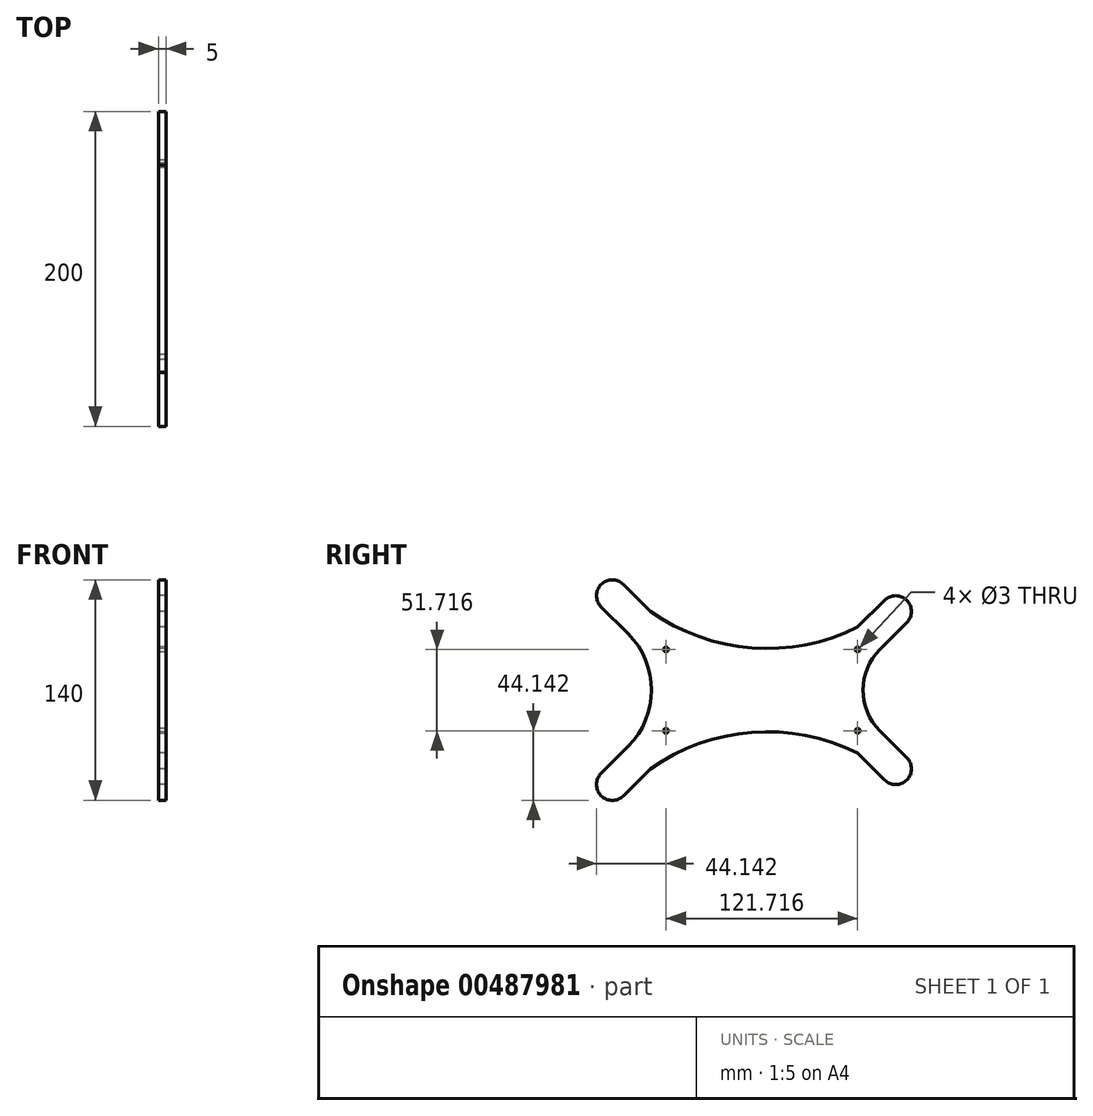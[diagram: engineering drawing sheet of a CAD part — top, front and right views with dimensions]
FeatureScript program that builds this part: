
annotation { "Feature Type Name" : "Feature", "Feature Type Description" : "" }
export const myFeature = defineFeature(function(context is Context, id is Id, definition is map)
    precondition{}
    {
        {
            var Q0;
            Q0=qCreatedBy(makeId("Right.planeOp"),FACE);
            var sketch = newSketch(context, id + "F0", { "sketchPlane" : qUnion([Q0])});
            skLineSegment(sketch, "E0", {"start": v(97.07, 42.93) * mm, "end": v(80, 25.86) * mm});
            skLineSegment(sketch, "E1", {"start": v(82.93, 57.07) * mm, "end": v(65.86, 40) * mm});
            skLineSegment(sketch, "E2.MirrorCS", {"start": v(97.07, -42.93) * mm, "end": v(80, -25.86) * mm});
            skLineSegment(sketch, "E3.MirrorCS", {"start": v(82.93, -57.07) * mm, "end": v(65.86, -40) * mm});
            skLineSegment(sketch, "E4", {"start": v(-82.93, 67.07) * mm, "end": v(-65.86, 50) * mm});
            skLineSegment(sketch, "E5", {"start": v(-97.07, 52.93) * mm, "end": v(-80, 35.86) * mm});
            skLineSegment(sketch, "E6.MirrorCS", {"start": v(-97.07, -52.93) * mm, "end": v(-80, -35.86) * mm});
            skLineSegment(sketch, "E7.MirrorCS", {"start": v(-82.93, -67.07) * mm, "end": v(-65.86, -50) * mm});
            skArc(sketch, "E8", {"start": v(65.86, -40) * mm, "mid": v(-1.38, -26.83) * mm, "end": v(-65.86, -50) * mm});
            skArc(sketch, "E9.MirrorCS", {"start": v(65.86, 40) * mm, "mid": v(-1.38, 26.83) * mm, "end": v(-65.86, 50) * mm});
            skArc(sketch, "E10", {"start": v(80, 25.86) * mm, "mid": v(69.29, 0) * mm, "end": v(80, -25.86) * mm});
            skArc(sketch, "E11", {"start": v(-80, -35.86) * mm, "mid": v(-65.15, 0) * mm, "end": v(-80, 35.86) * mm});
            skArc(sketch, "E12", {"start": v(82.93, -57.07) * mm, "mid": v(97.07, -57.07) * mm, "end": v(97.07, -42.93) * mm});
            skArc(sketch, "E13.MirrorCS", {"start": v(82.93, 57.07) * mm, "mid": v(97.07, 57.07) * mm, "end": v(97.07, 42.93) * mm});
            skArc(sketch, "E14", {"start": v(-97.07, -52.93) * mm, "mid": v(-97.07, -67.07) * mm, "end": v(-82.93, -67.07) * mm});
            skArc(sketch, "E15.MirrorCS", {"start": v(-97.07, 52.93) * mm, "mid": v(-97.07, 67.07) * mm, "end": v(-82.93, 67.07) * mm});
            skCircle(sketch, "E16", {"center": v(65.86, -25.86) * mm, "radius": 1.5 * mm});
            skCircle(sketch, "E17.MirrorC", {"center": v(65.86, 25.86) * mm, "radius": 1.5 * mm});
            skCircle(sketch, "E18", {"center": v(-55.86, -25.86) * mm, "radius": 1.5 * mm});
            skCircle(sketch, "E19.MirrorC", {"center": v(-55.86, 25.86) * mm, "radius": 1.5 * mm});
            skLineSegment(sketch, "E20", {"start": v(-54.36, -25.86) * mm, "end": v(64.36, -25.86) * mm});
            skSolve(sketch);
        }
        {
            var Q0;
            Q0=makeQuery(id+"F0.imprint","IMPRINT",FACE,{"disambiguationData":[TD([[makeQuery(id+"F0.imprint","IMPRINT",EDGE,{"derivedFrom":sQuery(id+"F0.wireOp",EDGE,"E0")}),-1.0]])]});
            extrude(context, id + "F1", {"entities" : qUnion([Q0]), "offsetDistance" : 25 * mm, "depth" : 5 * mm});
        }
    });
